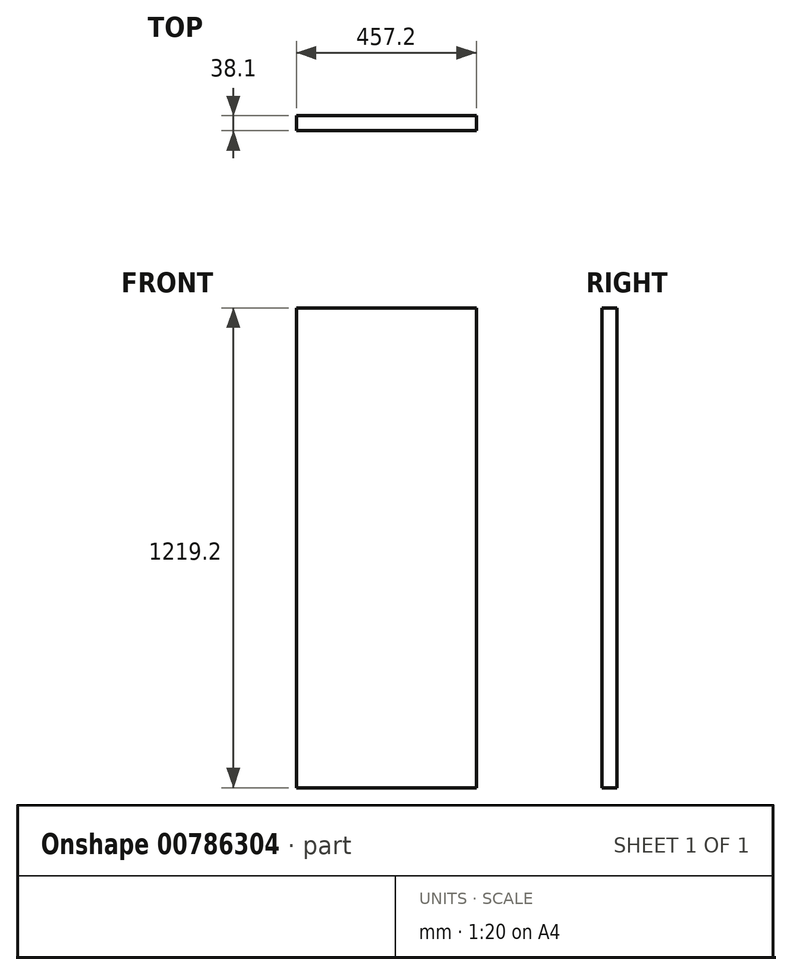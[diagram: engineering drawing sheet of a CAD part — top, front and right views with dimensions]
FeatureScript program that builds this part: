
annotation { "Feature Type Name" : "Feature", "Feature Type Description" : "" }
export const myFeature = defineFeature(function(context is Context, id is Id, definition is map)
    precondition{}
    {
        {
            var Q0;
            Q0=qCreatedBy(makeId("Front.planeOp"),FACE);
            var sketch = newSketch(context, id + "F0", { "sketchPlane" : qUnion([Q0])});
            skLineSegment(sketch, "E0.bottom", {"start": v(-228.6, 609.6) * mm, "end": v(228.6, 609.6) * mm});
            skLineSegment(sketch, "E0.top", {"start": v(-228.6, -609.6) * mm, "end": v(228.6, -609.6) * mm});
            skLineSegment(sketch, "E0.left", {"start": v(-228.6, 609.6) * mm, "end": v(-228.6, -609.6) * mm});
            skLineSegment(sketch, "E0.right", {"start": v(228.6, 609.6) * mm, "end": v(228.6, -609.6) * mm});
            skPoint(sketch, "E0.middle", {"position": v(0, 0) * mm});
            skSolve(sketch);
        }
        {
            var Q0;
            Q0=makeQuery(id+"F0.imprint","IMPRINT",FACE,{"disambiguationData":[TD([[makeQuery(id+"F0.imprint","IMPRINT",EDGE,{"derivedFrom":sQuery(id+"F0.wireOp",EDGE,"E0.bottom")}),-1.0]])]});
            extrude(context, id + "F1", {"entities" : qUnion([Q0]), "endBound" : BoundingType.SYMMETRIC, "depth" : 38.1 * mm, "offsetDistance" : 25.4 * mm});
        }
    });
